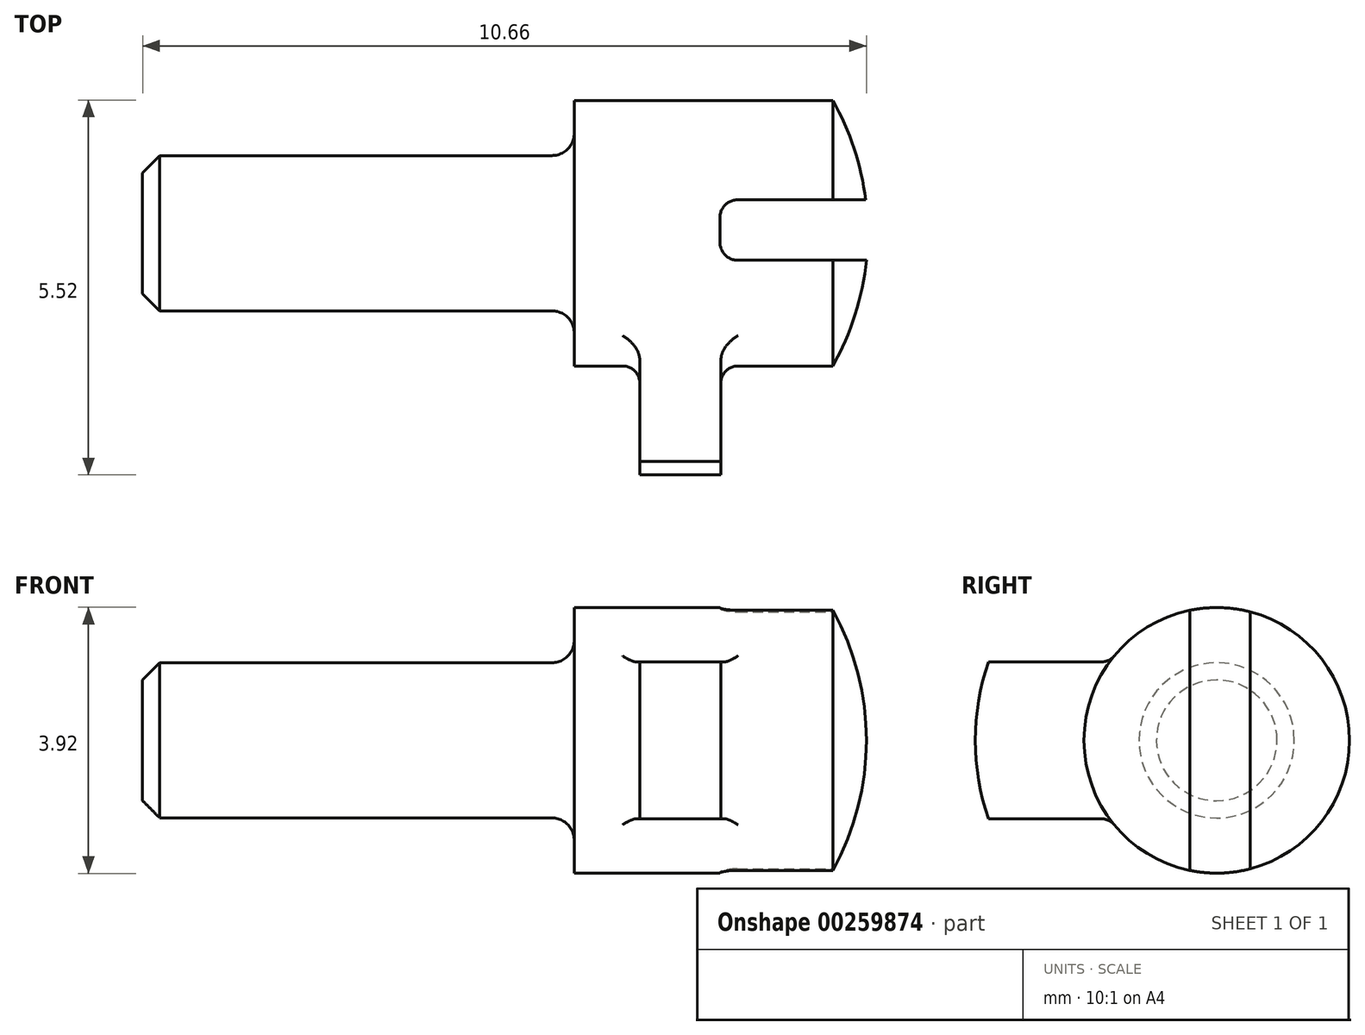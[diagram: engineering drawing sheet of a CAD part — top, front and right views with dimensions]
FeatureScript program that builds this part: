
annotation { "Feature Type Name" : "Feature", "Feature Type Description" : "" }
export const myFeature = defineFeature(function(context is Context, id is Id, definition is map)
    precondition{}
    {
        {
            var Q0;
            Q0=qCreatedBy(makeId("Top.planeOp"),FACE);
            var sketch = newSketch(context, id + "F0", { "sketchPlane" : qUnion([Q0])});
            skLineSegment(sketch, "E0.top", {"start": v(1.9, -1.96) * mm, "end": v(0.5, -1.96) * mm});
            skLineSegment(sketch, "E0.right", {"start": v(-1.9, -1.47) * mm, "end": v(-1.9, -1.96) * mm});
            skLineSegment(sketch, "E1.top", {"start": v(-2.23, -1.14) * mm, "end": v(-8.26, -1.14) * mm});
            skLineSegment(sketch, "E1.right", {"start": v(-8.26, 0) * mm, "end": v(-8.26, -1.14) * mm});
            skArc(sketch, "E2", {"start": v(1.9, -1.96) * mm, "mid": v(2.29, -1.01) * mm, "end": v(2.42, 0) * mm});
            skLineSegment(sketch, "E3", {"start": v(-0.94, -2.2) * mm, "end": v(-0.94, -3.56) * mm});
            skLineSegment(sketch, "E4", {"start": v(-0.94, -3.56) * mm, "end": v(0.25, -3.56) * mm});
            skLineSegment(sketch, "E5", {"start": v(0.25, -3.56) * mm, "end": v(0.25, -2.2) * mm});
            skLineSegment(sketch, "E6.trimOffspring", {"start": v(-1.2, -1.96) * mm, "end": v(-1.9, -1.96) * mm});
            skLineSegment(sketch, "E7", {"start": v(2.42, 0) * mm, "end": v(-8.26, 0) * mm});
            skPoint(sketch, "E8.visualSharp", {"position": v(-1.9, -1.14) * mm});
            skArc(sketch, "E8.filletArc", {"start": v(-1.9, -1.47) * mm, "mid": v(-2, -1.24) * mm, "end": v(-2.23, -1.14) * mm});
            skPoint(sketch, "E9.visualSharp", {"position": v(0.25, -1.96) * mm});
            skArc(sketch, "E9.filletArc", {"start": v(0.5, -1.96) * mm, "mid": v(0.33, -2.03) * mm, "end": v(0.25, -2.2) * mm});
            skPoint(sketch, "E10.visualSharp", {"position": v(-0.94, -1.96) * mm});
            skArc(sketch, "E10.filletArc", {"start": v(-0.94, -2.2) * mm, "mid": v(-1.01, -2.03) * mm, "end": v(-1.2, -1.96) * mm});
            skSolve(sketch);
        }
        {
            var Q0;
            Q0 = qSketchRegion(id + "F0", true);
            var Q1;
            Q1=sQuery(id+"F0.wireOp",EDGE,"E7");
            revolve(context, id + "F1", {"entities" : qUnion([Q0]), "axis" : qUnion([Q1]), "revolveType" : RevolveType.FULL});
        }
        {
            var Q0;
            Q0=qCreatedBy(makeId("Top.planeOp"),FACE);
            var sketch = newSketch(context, id + "F2", { "sketchPlane" : qUnion([Q0])});
            skLineSegment(sketch, "E11.bottom", {"start": v(0.5, 0.5) * mm, "end": v(2.63, 0.5) * mm});
            skLineSegment(sketch, "E11.top", {"start": v(0.5, -0.4) * mm, "end": v(2.63, -0.4) * mm});
            skLineSegment(sketch, "E11.left", {"start": v(0.24, 0.24) * mm, "end": v(0.24, -0.14) * mm});
            skLineSegment(sketch, "E11.right", {"start": v(2.63, 0.5) * mm, "end": v(2.63, -0.4) * mm});
            skPoint(sketch, "E12.visualSharp", {"position": v(0.24, 0.5) * mm});
            skArc(sketch, "E12.filletArc", {"start": v(0.5, 0.5) * mm, "mid": v(0.32, 0.42) * mm, "end": v(0.24, 0.24) * mm});
            skPoint(sketch, "E13.visualSharp", {"position": v(0.24, -0.4) * mm});
            skArc(sketch, "E13.filletArc", {"start": v(0.24, -0.14) * mm, "mid": v(0.32, -0.32) * mm, "end": v(0.5, -0.4) * mm});
            skSolve(sketch);
        }
        {
            var Q0;
            Q0 = qSketchRegion(id + "F2", true);
            extrude(context, id + "F3", {"entities" : qUnion([Q0]), "operationType" : NewBodyOperationType.REMOVE, "oppositeDirection" : true, "depth" : 25.4 * mm, "hasSecondDirection" : true, "secondDirectionOppositeDirection" : false, "secondDirectionDepth" : 25.4 * mm});
        }
        {
            var Q0;
            Q0=makeQuery(id+"F1.opRevolve","SWEPT_EDGE",EDGE,{"disambiguationData":[OSD([sQuery(id+"F0.wireOp",EDGE,"E1.top"),sQuery(id+"F0.wireOp",EDGE,"E1.right")])]});
            chamfer(context, id + "F4", {"entities" : qUnion([Q0]), "chamferType" : ChamferType.OFFSET_ANGLE, "width" : 0.25 * mm, "oppositeDirection" : false, "angle" : 45 * degree, "tangentPropagation" : true});
        }
        {
            var Q0;
            Q0=qCreatedBy(makeId("Right.planeOp"),FACE);
            var sketch = newSketch(context, id + "F5", { "sketchPlane" : qUnion([Q0])});
            skArc(sketch, "E14", {"start": v(-1.58, -1.16) * mm, "mid": v(1.96, 0) * mm, "end": v(-1.58, 1.16) * mm});
            skArc(sketch, "E15", {"start": v(-3.36, -1.16) * mm, "mid": v(3.56, 0) * mm, "end": v(-3.36, 1.16) * mm});
            skLineSegment(sketch, "E16", {"start": v(-3.36, 1.16) * mm, "end": v(-1.58, 1.16) * mm});
            skLineSegment(sketch, "E17", {"start": v(-1.58, -1.16) * mm, "end": v(-3.36, -1.16) * mm});
            skSolve(sketch);
        }
        {
            var Q0;
            Q0 = qSketchRegion(id + "F5", true);
            extrude(context, id + "F6", {"entities" : qUnion([Q0]), "operationType" : NewBodyOperationType.REMOVE, "oppositeDirection" : true, "depth" : 25.4 * mm, "hasSecondDirection" : true, "secondDirectionOppositeDirection" : false, "secondDirectionDepth" : 25.4 * mm});
        }
        {
            var Q0;
            Q0=makeQuery(id+"F6.boolean.opBoolean","COPY",EDGE,{"derivedFrom":makeQuery(id+"F6.opExtrude","SWEPT_EDGE",EDGE,{"disambiguationData":[OSD([sQuery(id+"F5.wireOp",EDGE,"E14"),sQuery(id+"F5.wireOp",EDGE,"E16")])]})});
            var Q1;
            Q1=makeQuery(id+"F6.boolean.opBoolean","COPY",EDGE,{"derivedFrom":makeQuery(id+"F6.opExtrude","SWEPT_EDGE",EDGE,{"disambiguationData":[OSD([sQuery(id+"F5.wireOp",EDGE,"E14"),sQuery(id+"F5.wireOp",EDGE,"E17")])]})});
            fillet(context, id + "F7", {"entities" : qUnion([Q0, Q1]), "radius" : 0.25 * mm, "tangentPropagation" : true, "allowEdgeOverflow" : false});
        }
    });
